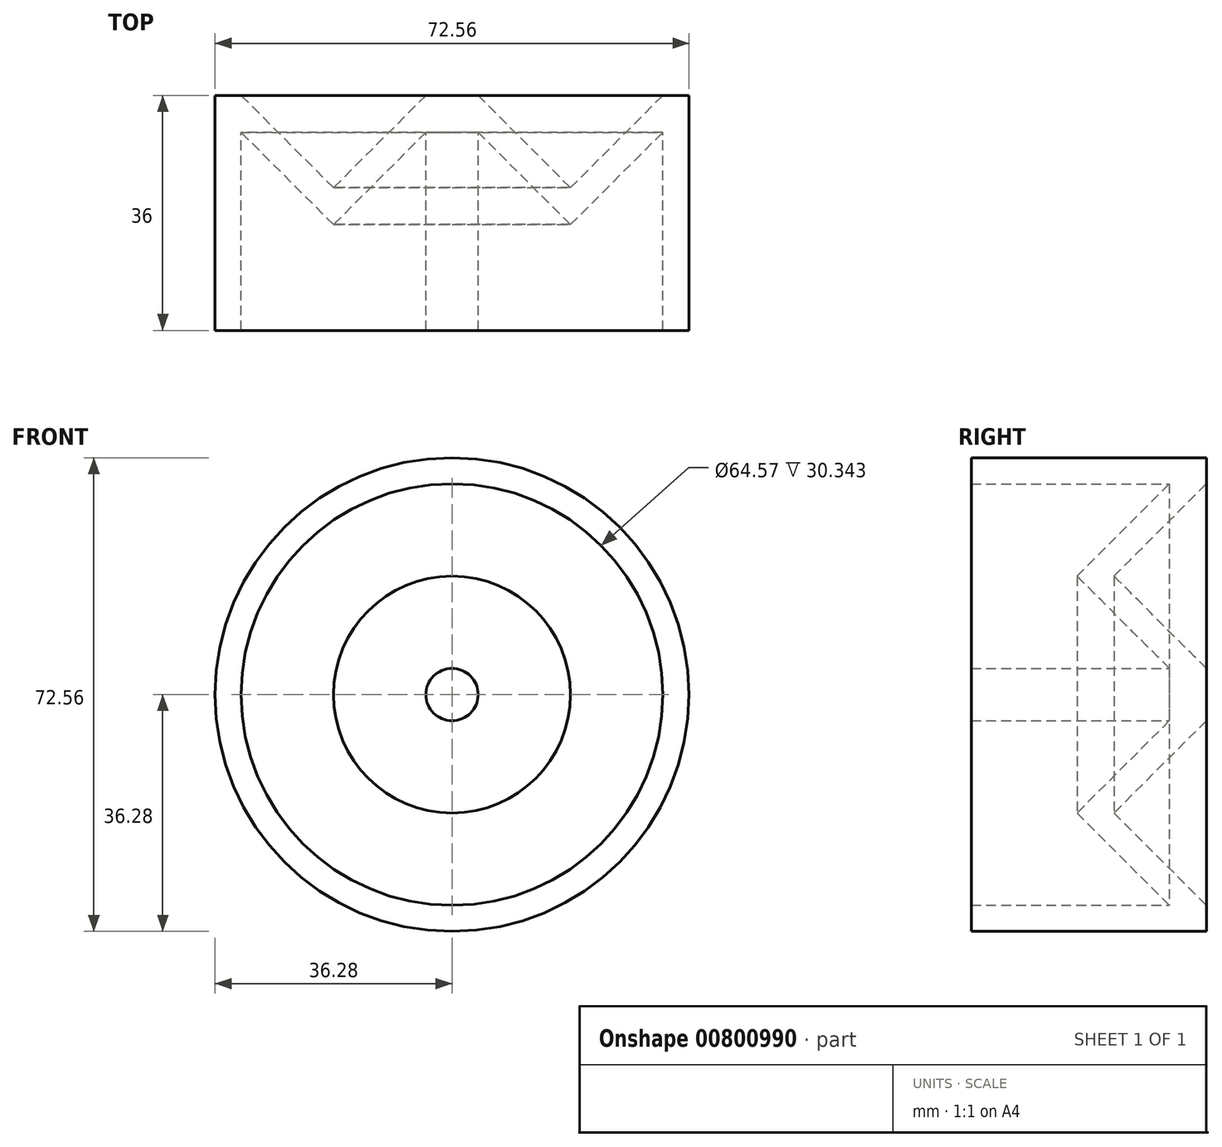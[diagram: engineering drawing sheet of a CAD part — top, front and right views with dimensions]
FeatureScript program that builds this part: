
annotation { "Feature Type Name" : "Feature", "Feature Type Description" : "" }
export const myFeature = defineFeature(function(context is Context, id is Id, definition is map)
    precondition{}
    {
        {
            var Q0;
            Q0=qCreatedBy(makeId("Top.planeOp"),FACE);
            var sketch = newSketch(context, id + "F0", { "sketchPlane" : qUnion([Q0])});
            skLineSegment(sketch, "E0", {"start": v(0, 0) * mm, "end": v(0, -36) * mm});
            skLineSegment(sketch, "E1", {"start": v(0, -36) * mm, "end": v(4, -36) * mm});
            skLineSegment(sketch, "E2", {"start": v(4, -36) * mm, "end": v(4, -5.66) * mm});
            skLineSegment(sketch, "E3", {"start": v(4, -5.66) * mm, "end": v(18.14, -19.8) * mm});
            skLineSegment(sketch, "E4", {"start": v(18.14, -19.8) * mm, "end": v(32.28, -5.66) * mm});
            skLineSegment(sketch, "E5", {"start": v(32.28, -5.66) * mm, "end": v(32.28, -36) * mm});
            skLineSegment(sketch, "E6", {"start": v(32.28, -36) * mm, "end": v(36.28, -36) * mm});
            skLineSegment(sketch, "E7", {"start": v(36.28, -36) * mm, "end": v(36.28, 0) * mm});
            skLineSegment(sketch, "E8", {"start": v(36.28, 0) * mm, "end": v(32.28, 0) * mm});
            skLineSegment(sketch, "E9", {"start": v(32.28, 0) * mm, "end": v(18.14, -14.14) * mm});
            skLineSegment(sketch, "E10", {"start": v(18.14, -14.14) * mm, "end": v(4, 0) * mm});
            skLineSegment(sketch, "E11", {"start": v(4, 0) * mm, "end": v(0, 0) * mm});
            skLineSegment(sketch, "E12", {"start": v(18.14, -14.14) * mm, "end": v(18.14, -19.8) * mm, "construction": true});
            skSolve(sketch);
        }
        {
            var Q0;
            Q0=makeQuery(id+"F0.imprint","IMPRINT",FACE,{"disambiguationData":[TD([[makeQuery(id+"F0.imprint","IMPRINT",EDGE,{"derivedFrom":sQuery(id+"F0.wireOp",EDGE,"E0")}),1.0]])]});
            var Q1;
            Q1=sQuery(id+"F0.wireOp",EDGE,"E0");
            revolve(context, id + "F1", {"surfaceOperationType" : NewSurfaceOperationType.NEW, "entities" : qUnion([Q0]), "axis" : qUnion([Q1]), "revolveType" : RevolveType.FULL});
        }
    });
